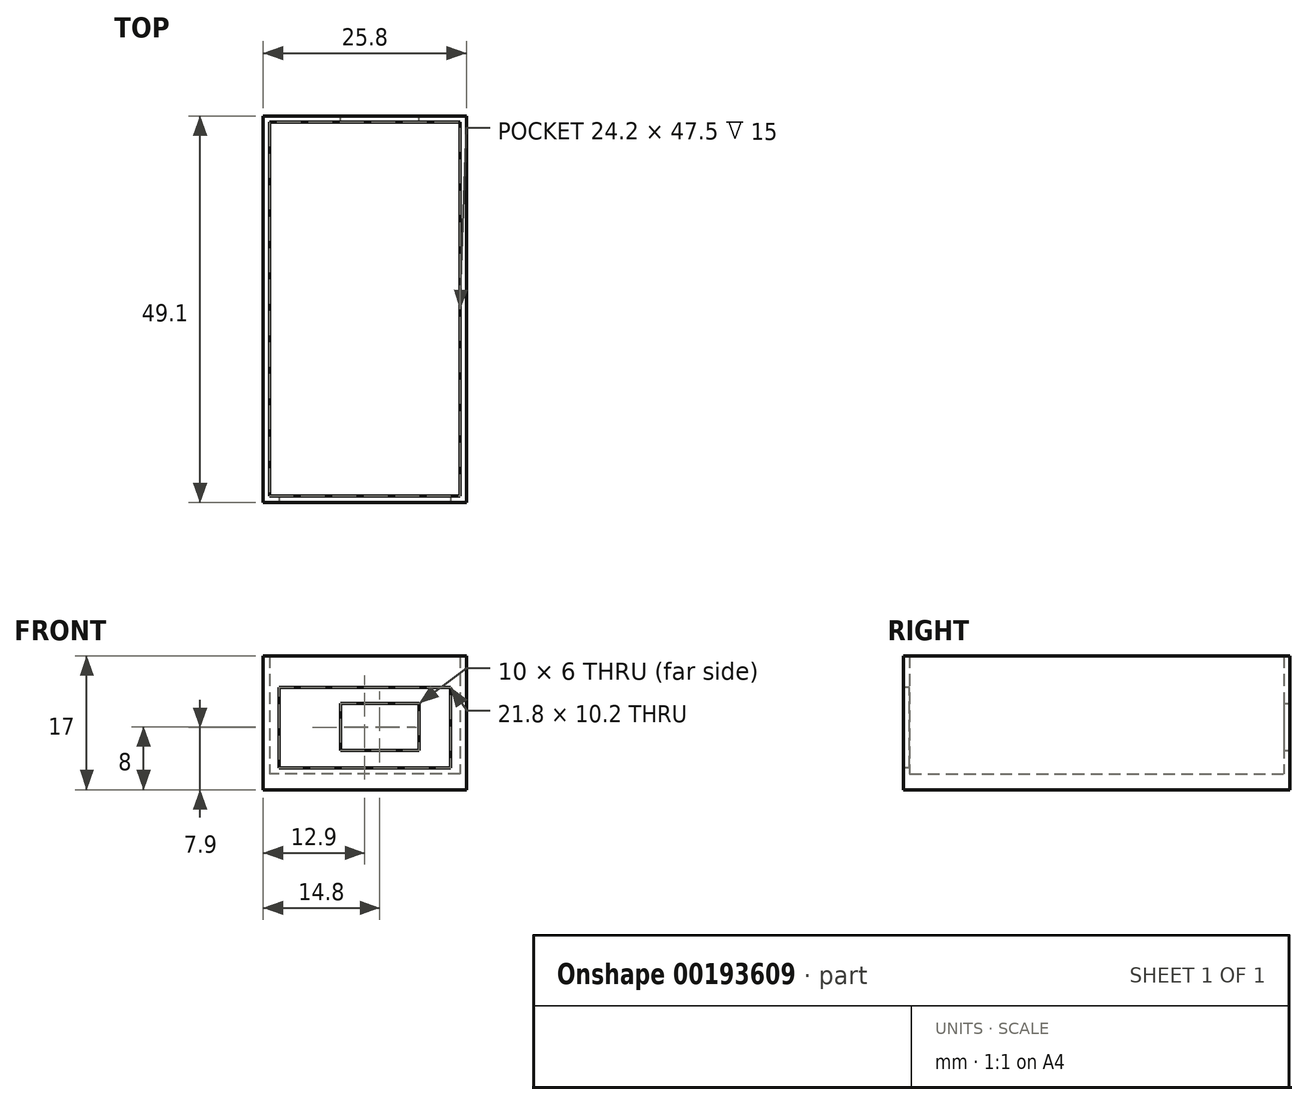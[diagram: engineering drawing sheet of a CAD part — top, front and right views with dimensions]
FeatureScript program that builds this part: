
annotation { "Feature Type Name" : "Feature", "Feature Type Description" : "" }
export const myFeature = defineFeature(function(context is Context, id is Id, definition is map)
    precondition{}
    {
        {
            var Q0;
            Q0=qCreatedBy(makeId("Top.planeOp"),FACE);
            var sketch = newSketch(context, id + "F0", { "sketchPlane" : qUnion([Q0])});
            skLineSegment(sketch, "E0.bottom", {"start": v(12.1, -23.75) * mm, "end": v(-12.1, -23.75) * mm});
            skLineSegment(sketch, "E0.top", {"start": v(12.1, 23.75) * mm, "end": v(-12.1, 23.75) * mm});
            skLineSegment(sketch, "E0.left", {"start": v(12.1, -23.75) * mm, "end": v(12.1, 23.75) * mm});
            skLineSegment(sketch, "E0.right", {"start": v(-12.1, -23.75) * mm, "end": v(-12.1, 23.75) * mm});
            skPoint(sketch, "E0.middle", {"position": v(0, 0) * mm});
            skLineSegment(sketch, "E1.0", {"start": v(-12.9, -24.55) * mm, "end": v(-12.9, 24.55) * mm});
            skLineSegment(sketch, "E1.1", {"start": v(12.9, -24.55) * mm, "end": v(-12.9, -24.55) * mm});
            skLineSegment(sketch, "E1.2", {"start": v(12.9, -24.55) * mm, "end": v(12.9, 24.55) * mm});
            skLineSegment(sketch, "E1.3", {"start": v(12.9, 24.55) * mm, "end": v(-12.9, 24.55) * mm});
            skSolve(sketch);
        }
        {
            var Q0;
            Q0 = qSketchRegion(id + "F0", true);
            var Q1;
            Q1=makeQuery(id+"F0.imprint","IMPRINT",FACE,{"disambiguationData":[TD([[makeQuery(id+"F0.imprint","IMPRINT",EDGE,{"derivedFrom":sQuery(id+"F0.wireOp",EDGE,"E0.bottom")}),-1.0]])]});
            extrude(context, id + "F1", {"entities" : qUnion([Q0, Q1]), "depth" : 2 * mm, "offsetDistance" : 25 * mm});
        }
        {
            var Q0;
            Q0=makeQuery(id+"F1.opExtrude","CAP_FACE",FACE,{"disambiguationData":[OSD([sQuery(id+"F0.wireOp",EDGE,"E1.0"),sQuery(id+"F0.wireOp",EDGE,"E1.1"),sQuery(id+"F0.wireOp",EDGE,"E1.2"),sQuery(id+"F0.wireOp",EDGE,"E1.3")])],"isStart":false});
            var sketch = newSketch(context, id + "F2", { "sketchPlane" : qUnion([Q0])});
            skLineSegment(sketch, "E2.0", {"start": v(-12.1, -23.75) * mm, "end": v(-12.1, 23.75) * mm});
            skLineSegment(sketch, "E3.0", {"start": v(-12.9, -24.55) * mm, "end": v(-12.9, 24.55) * mm});
            skLineSegment(sketch, "E4.0", {"start": v(12.1, -23.75) * mm, "end": v(-12.1, -23.75) * mm});
            skLineSegment(sketch, "E4.1", {"start": v(12.1, 23.75) * mm, "end": v(-12.1, 23.75) * mm});
            skLineSegment(sketch, "E4.2", {"start": v(12.1, -23.75) * mm, "end": v(12.1, 23.75) * mm});
            skLineSegment(sketch, "E4.3", {"start": v(12.9, -24.55) * mm, "end": v(-12.9, -24.55) * mm});
            skLineSegment(sketch, "E4.4", {"start": v(12.9, -24.55) * mm, "end": v(12.9, 24.55) * mm});
            skLineSegment(sketch, "E4.5", {"start": v(12.9, 24.55) * mm, "end": v(-12.9, 24.55) * mm});
            skSolve(sketch);
        }
        {
            var Q0;
            Q0 = qSketchRegion(id + "F2", true);
            extrude(context, id + "F3", {"entities" : qUnion([Q0]), "operationType" : NewBodyOperationType.ADD, "depth" : 15 * mm, "offsetDistance" : 25 * mm});
        }
        {
            var Q0;
            Q0=makeQuery(id+"F3.boolean.opBoolean","MERGE",FACE,{"derivedFrom":[makeQuery(id+"F1.opExtrude","SWEPT_FACE",FACE,{"disambiguationData":[OSD([sQuery(id+"F0.wireOp",EDGE,"E1.1")])]}),makeQuery(id+"F3.opExtrude","SWEPT_FACE",FACE,{"disambiguationData":[OSD([sQuery(id+"F2.wireOp",EDGE,"E4.3")])]})]});
            var sketch = newSketch(context, id + "F4", { "sketchPlane" : qUnion([Q0])});
            skLineSegment(sketch, "E5.0", {"start": v(12.9, 2) * mm, "end": v(-12.9, 2) * mm});
            skLineSegment(sketch, "E6.bottom", {"start": v(-10.9, 13) * mm, "end": v(10.9, 13) * mm});
            skLineSegment(sketch, "E6.top", {"start": v(-10.9, 2.8) * mm, "end": v(10.9, 2.8) * mm});
            skLineSegment(sketch, "E6.left", {"start": v(-10.9, 13) * mm, "end": v(-10.9, 2.8) * mm});
            skLineSegment(sketch, "E6.right", {"start": v(10.9, 13) * mm, "end": v(10.9, 2.8) * mm});
            skSolve(sketch);
        }
        {
            var Q0;
            Q0=makeQuery(id+"F4.imprint","IMPRINT",FACE,{"disambiguationData":[TD([[makeQuery(id+"F4.imprint","IMPRINT",EDGE,{"derivedFrom":sQuery(id+"F4.wireOp",EDGE,"E6.bottom")}),-1.0]])]});
            extrude(context, id + "F5", {"entities" : qUnion([Q0]), "operationType" : NewBodyOperationType.REMOVE, "endBound" : BoundingType.UP_TO_NEXT, "oppositeDirection" : true, "depth" : 25 * mm, "offsetDistance" : 25 * mm});
        }
        {
            var Q0;
            Q0=makeQuery(id+"F3.boolean.opBoolean","MERGE",FACE,{"derivedFrom":[makeQuery(id+"F1.opExtrude","SWEPT_FACE",FACE,{"disambiguationData":[OSD([sQuery(id+"F0.wireOp",EDGE,"E1.3")])]}),makeQuery(id+"F3.opExtrude","SWEPT_FACE",FACE,{"disambiguationData":[OSD([sQuery(id+"F2.wireOp",EDGE,"E4.5")])]})]});
            var sketch = newSketch(context, id + "F6", { "sketchPlane" : qUnion([Q0])});
            skLineSegment(sketch, "E7.bottom", {"start": v(-6.9, 11) * mm, "end": v(3.1, 11) * mm});
            skLineSegment(sketch, "E7.top", {"start": v(-6.9, 5) * mm, "end": v(3.1, 5) * mm});
            skLineSegment(sketch, "E7.left", {"start": v(-6.9, 11) * mm, "end": v(-6.9, 5) * mm});
            skLineSegment(sketch, "E7.right", {"start": v(3.1, 11) * mm, "end": v(3.1, 5) * mm});
            skSolve(sketch);
        }
        {
            var Q0;
            Q0 = qSketchRegion(id + "F6", true);
            extrude(context, id + "F7", {"entities" : qUnion([Q0]), "operationType" : NewBodyOperationType.REMOVE, "endBound" : BoundingType.UP_TO_NEXT, "oppositeDirection" : true, "depth" : 25 * mm, "offsetDistance" : 25 * mm});
        }
    });
